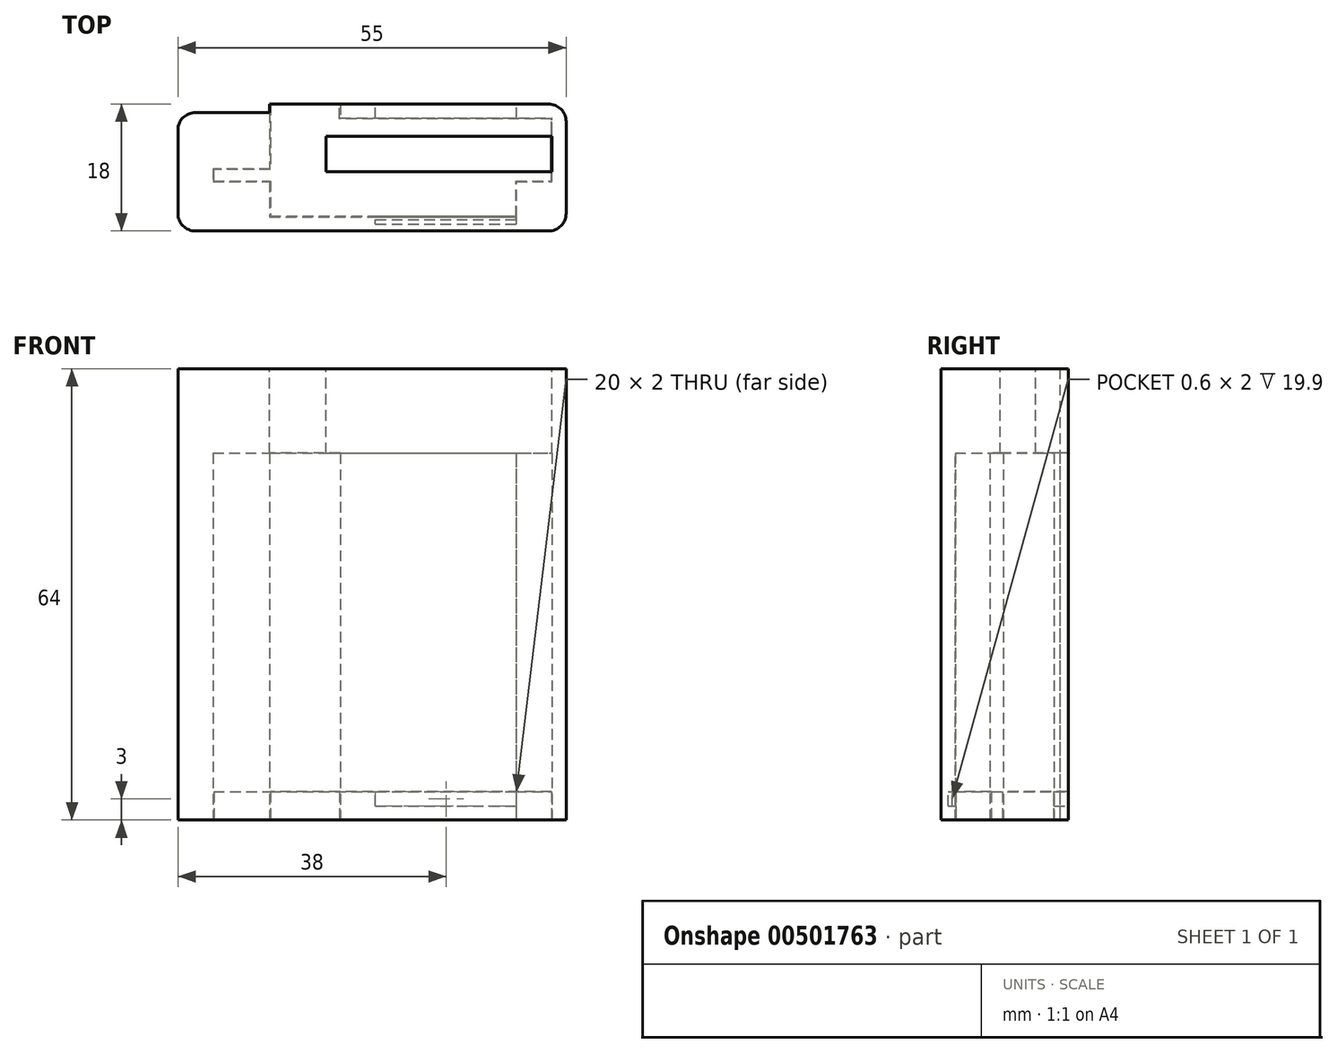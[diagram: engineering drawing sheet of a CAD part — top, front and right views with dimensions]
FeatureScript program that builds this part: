
annotation { "Feature Type Name" : "Feature", "Feature Type Description" : "" }
export const myFeature = defineFeature(function(context is Context, id is Id, definition is map)
    precondition{}
    {
        {
            var Q0;
            Q0=qCreatedBy(makeId("Top.planeOp"),FACE);
            var sketch = newSketch(context, id + "F0", { "sketchPlane" : qUnion([Q0])});
            skLineSegment(sketch, "E0", {"start": v(0, 0) * mm, "end": v(0, 8) * mm});
            skLineSegment(sketch, "E1", {"start": v(0, 8) * mm, "end": v(-8, 8) * mm});
            skLineSegment(sketch, "E2", {"start": v(0, 0) * mm, "end": v(-8, 0) * mm});
            skLineSegment(sketch, "E3", {"start": v(-8, 0) * mm, "end": v(-8, -1.8) * mm});
            skLineSegment(sketch, "E4", {"start": v(-8, -1.8) * mm, "end": v(0, -1.8) * mm});
            skLineSegment(sketch, "E5", {"start": v(0, -1.8) * mm, "end": v(0, -6.8) * mm});
            skLineSegment(sketch, "E6", {"start": v(-8, 8) * mm, "end": v(-13, 8) * mm});
            skLineSegment(sketch, "E7", {"start": v(-13, 8) * mm, "end": v(-13, -6.8) * mm});
            skLineSegment(sketch, "E8", {"start": v(-13, -6.8) * mm, "end": v(-13, -8.8) * mm});
            skLineSegment(sketch, "E9", {"start": v(0, -6.8) * mm, "end": v(40, -6.8) * mm});
            skLineSegment(sketch, "E10", {"start": v(40, -6.8) * mm, "end": v(40, 7.2) * mm});
            skLineSegment(sketch, "E11", {"start": v(0, 0) * mm, "end": v(10, 0) * mm, "construction": true});
            skLineSegment(sketch, "E12", {"start": v(10, 0) * mm, "end": v(10, 7.2) * mm});
            skLineSegment(sketch, "E13", {"start": v(10, 7.2) * mm, "end": v(40, 7.2) * mm});
            skLineSegment(sketch, "E14", {"start": v(-13, -8.8) * mm, "end": v(42, -8.8) * mm});
            skLineSegment(sketch, "E15", {"start": v(42, -8.8) * mm, "end": v(42, 9.2) * mm});
            skLineSegment(sketch, "E16", {"start": v(42, 9.2) * mm, "end": v(10, 9.2) * mm});
            skLineSegment(sketch, "E17", {"start": v(10, 9.2) * mm, "end": v(10, 7.2) * mm});
            skSolve(sketch);
        }
        {
            var Q0;
            Q0=makeQuery(id+"F0.imprint","IMPRINT",FACE,{"disambiguationData":[TD([[makeQuery(id+"F0.imprint","IMPRINT",EDGE,{"derivedFrom":sQuery(id+"F0.wireOp",EDGE,"E0")}),1.0]])]});
            extrude(context, id + "F1", {"entities" : qUnion([Q0]), "depth" : 60 * mm});
        }
        {
            var Q0;
            Q0=makeQuery(id+"F1.opExtrude","CAP_FACE",FACE,{"disambiguationData":[OSD([sQuery(id+"F0.wireOp",EDGE,"E0"),sQuery(id+"F0.wireOp",EDGE,"E1"),sQuery(id+"F0.wireOp",EDGE,"E2"),sQuery(id+"F0.wireOp",EDGE,"E3"),sQuery(id+"F0.wireOp",EDGE,"E4"),sQuery(id+"F0.wireOp",EDGE,"E5"),sQuery(id+"F0.wireOp",EDGE,"E6"),sQuery(id+"F0.wireOp",EDGE,"E7"),sQuery(id+"F0.wireOp",EDGE,"E8"),sQuery(id+"F0.wireOp",EDGE,"E9"),sQuery(id+"F0.wireOp",EDGE,"E10"),sQuery(id+"F0.wireOp",EDGE,"E13"),sQuery(id+"F0.wireOp",EDGE,"E14"),sQuery(id+"F0.wireOp",EDGE,"E15"),sQuery(id+"F0.wireOp",EDGE,"E16"),sQuery(id+"F0.wireOp",EDGE,"E17")])],"isStart":false});
            var sketch = newSketch(context, id + "F2", { "sketchPlane" : qUnion([Q0])});
            skLineSegment(sketch, "E18", {"start": v(8, -0.4) * mm, "end": v(40, -0.4) * mm});
            skLineSegment(sketch, "E19", {"start": v(8, -0.4) * mm, "end": v(8, 4.6) * mm});
            skLineSegment(sketch, "E20", {"start": v(8, 4.6) * mm, "end": v(40, 4.6) * mm});
            skLineSegment(sketch, "E21", {"start": v(40, 4.6) * mm, "end": v(40, -0.4) * mm});
            skLineSegment(sketch, "E22", {"start": v(10, 9.2) * mm, "end": v(0, 9.2) * mm});
            skLineSegment(sketch, "E23", {"start": v(0, 9.2) * mm, "end": v(0, 8) * mm});
            skSolve(sketch);
        }
        {
            var Q0;
            {var subQ0=sQuery(id+"F2.wireOp",EDGE,"E18");Q0=makeQuery(id+"F2.imprint","IMPRINT",FACE,{"disambiguationData":[TD([[makeQuery(id+"F2.imprint","IMPRINT",EDGE,{"derivedFrom":subQ0}),-1.0]])]});}
            extrude(context, id + "F3", {"entities" : qUnion([Q0]), "operationType" : NewBodyOperationType.ADD, "oppositeDirection" : true, "depth" : 12 * mm});
        }
        {
            var Q0;
            Q0=makeQuery(id+"F1.opExtrude","SWEPT_EDGE",EDGE,{"disambiguationData":[OSD([sQuery(id+"F0.wireOp",EDGE,"E15"),sQuery(id+"F0.wireOp",EDGE,"E16")])]});
            var Q1;
            Q1=makeQuery(id+"F1.opExtrude","SWEPT_EDGE",EDGE,{"disambiguationData":[OSD([sQuery(id+"F0.wireOp",EDGE,"E14"),sQuery(id+"F0.wireOp",EDGE,"E15")])]});
            var Q2;
            Q2=makeQuery(id+"F1.opExtrude","SWEPT_EDGE",EDGE,{"disambiguationData":[OSD([sQuery(id+"F0.wireOp",EDGE,"E8"),sQuery(id+"F0.wireOp",EDGE,"E14")])]});
            var Q3;
            Q3=makeQuery(id+"F1.opExtrude","SWEPT_EDGE",EDGE,{"disambiguationData":[OSD([sQuery(id+"F0.wireOp",EDGE,"E6"),sQuery(id+"F0.wireOp",EDGE,"E7")])]});
            fillet(context, id + "F4", {"entities" : qUnion([Q0, Q1, Q2, Q3]), "radius" : 2.5 * mm, "tangentPropagation" : true, "allowEdgeOverflow" : false});
        }
        {
            var Q0;
            Q0=makeQuery(id+"F1.opExtrude","CAP_FACE",FACE,{"disambiguationData":[OSD([sQuery(id+"F0.wireOp",EDGE,"E0"),sQuery(id+"F0.wireOp",EDGE,"E1"),sQuery(id+"F0.wireOp",EDGE,"E2"),sQuery(id+"F0.wireOp",EDGE,"E3"),sQuery(id+"F0.wireOp",EDGE,"E4"),sQuery(id+"F0.wireOp",EDGE,"E5"),sQuery(id+"F0.wireOp",EDGE,"E6"),sQuery(id+"F0.wireOp",EDGE,"E7"),sQuery(id+"F0.wireOp",EDGE,"E8"),sQuery(id+"F0.wireOp",EDGE,"E9"),sQuery(id+"F0.wireOp",EDGE,"E10"),sQuery(id+"F0.wireOp",EDGE,"E13"),sQuery(id+"F0.wireOp",EDGE,"E14"),sQuery(id+"F0.wireOp",EDGE,"E15"),sQuery(id+"F0.wireOp",EDGE,"E16"),sQuery(id+"F0.wireOp",EDGE,"E17")])],"isStart":true});
            extrude(context, id + "F5", {"entities" : qUnion([Q0]), "operationType" : NewBodyOperationType.ADD, "depth" : 4 * mm});
        }
        {
            var Q0;
            Q0=makeQuery(id+"F3.opExtrude","CAP_FACE",FACE,{"disambiguationData":[OSD([sQuery(id+"F0.wireOp",EDGE,"E0"),sQuery(id+"F0.wireOp",EDGE,"E2"),sQuery(id+"F0.wireOp",EDGE,"E3"),sQuery(id+"F0.wireOp",EDGE,"E4"),sQuery(id+"F0.wireOp",EDGE,"E5"),sQuery(id+"F0.wireOp",EDGE,"E9"),sQuery(id+"F0.wireOp",EDGE,"E10"),sQuery(id+"F0.wireOp",EDGE,"E13"),sQuery(id+"F0.wireOp",EDGE,"E17"),sQuery(id+"F2.wireOp",EDGE,"E18"),sQuery(id+"F2.wireOp",EDGE,"E19"),sQuery(id+"F2.wireOp",EDGE,"E20"),sQuery(id+"F2.wireOp",EDGE,"E22"),sQuery(id+"F2.wireOp",EDGE,"E23")])],"isStart":false});
            var sketch = newSketch(context, id + "F6", { "sketchPlane" : qUnion([Q0])});
            skLineSegment(sketch, "E24", {"start": v(35, 6.8) * mm, "end": v(35, 1.8) * mm});
            skLineSegment(sketch, "E25.0", {"start": v(0, 1.8) * mm, "end": v(0, 6.8) * mm});
            skLineSegment(sketch, "E26", {"start": v(35, 1.8) * mm, "end": v(40, 1.8) * mm});
            skSolve(sketch);
        }
        {
            var Q0;
            {var subQ0=sQuery(id+"F6.wireOp",EDGE,"E24");Q0=makeQuery(id+"F6.imprint","IMPRINT",FACE,{"disambiguationData":[TD([[makeQuery(id+"F6.imprint","IMPRINT",EDGE,{"derivedFrom":subQ0}),1.0]])]});}
            extrude(context, id + "F7", {"entities" : qUnion([Q0]), "operationType" : NewBodyOperationType.ADD, "depth" : 52 * mm});
        }
        {
            var Q0;
            {var subQ0=sQuery(id+"F0.wireOp",EDGE,"E16");Q0=makeQuery(id+"F5.boolean.opBoolean","MERGE",FACE,{"derivedFrom":[makeQuery(id+"F3.boolean.opBoolean","MERGE",FACE,{"derivedFrom":[makeQuery(id+"F1.opExtrude","SWEPT_FACE",FACE,{"disambiguationData":[OSD([subQ0])]}),makeQuery(id+"F3.opExtrude","SWEPT_FACE",FACE,{"disambiguationData":[OSD([sQuery(id+"F2.wireOp",EDGE,"E22")])]})]}),makeQuery(id+"F5.opExtrude","SWEPT_FACE",FACE,{"disambiguationData":[OSD([subQ0])]})]});}
            var sketch = newSketch(context, id + "F8", { "sketchPlane" : qUnion([Q0])});
            skLineSegment(sketch, "E27.bottom", {"start": v(-15, -2) * mm, "end": v(-35, -2) * mm});
            skLineSegment(sketch, "E27.top", {"start": v(-15, 0) * mm, "end": v(-35, 0) * mm});
            skLineSegment(sketch, "E27.left", {"start": v(-15, -2) * mm, "end": v(-15, 0) * mm});
            skLineSegment(sketch, "E27.right", {"start": v(-35, -2) * mm, "end": v(-35, 0) * mm});
            skSolve(sketch);
        }
        {
            var Q0;
            Q0 = qSketchRegion(id + "F8", true);
            extrude(context, id + "F9", {"entities" : qUnion([Q0]), "operationType" : NewBodyOperationType.REMOVE, "oppositeDirection" : true, "depth" : 17 * mm});
        }
        {
            var Q0;
            {var subQ0=sQuery(id+"F0.wireOp",EDGE,"E16");Q0=makeQuery(id+"F5.boolean.opBoolean","MERGE",FACE,{"derivedFrom":[makeQuery(id+"F3.boolean.opBoolean","MERGE",FACE,{"derivedFrom":[makeQuery(id+"F1.opExtrude","SWEPT_FACE",FACE,{"disambiguationData":[OSD([subQ0])]}),makeQuery(id+"F3.opExtrude","SWEPT_FACE",FACE,{"disambiguationData":[OSD([sQuery(id+"F2.wireOp",EDGE,"E22")])]})]}),makeQuery(id+"F5.opExtrude","SWEPT_FACE",FACE,{"disambiguationData":[OSD([subQ0])]})]});}
            var sketch = newSketch(context, id + "F10", { "sketchPlane" : qUnion([Q0])});
            skLineSegment(sketch, "E28.bottom", {"start": v(-35, 0) * mm, "end": v(-15, 0) * mm});
            skLineSegment(sketch, "E28.top", {"start": v(-35, -2) * mm, "end": v(-15, -2) * mm});
            skLineSegment(sketch, "E28.left", {"start": v(-35, 0) * mm, "end": v(-35, -2) * mm});
            skLineSegment(sketch, "E28.right", {"start": v(-15, 0) * mm, "end": v(-15, -2) * mm});
            skSolve(sketch);
        }
        {
            var Q0;
            {var subQ0=sQuery(id+"F0.wireOp",EDGE,"E10");var subQ1=sQuery(id+"F0.wireOp",EDGE,"E9");Q0=makeQuery(id+"F7.boolean.opBoolean","MERGE",FACE,{"derivedFrom":[makeQuery(id+"F5.opExtrude","CAP_FACE",FACE,{"disambiguationData":[OSD([sQuery(id+"F0.wireOp",EDGE,"E0"),sQuery(id+"F0.wireOp",EDGE,"E1"),sQuery(id+"F0.wireOp",EDGE,"E2"),sQuery(id+"F0.wireOp",EDGE,"E3"),sQuery(id+"F0.wireOp",EDGE,"E4"),sQuery(id+"F0.wireOp",EDGE,"E5"),sQuery(id+"F0.wireOp",EDGE,"E6"),sQuery(id+"F0.wireOp",EDGE,"E7"),sQuery(id+"F0.wireOp",EDGE,"E8"),subQ1,subQ0,sQuery(id+"F0.wireOp",EDGE,"E13"),sQuery(id+"F0.wireOp",EDGE,"E14"),sQuery(id+"F0.wireOp",EDGE,"E15"),sQuery(id+"F0.wireOp",EDGE,"E16"),sQuery(id+"F0.wireOp",EDGE,"E17")])],"isStart":false}),makeQuery(id+"F7.opExtrude","CAP_FACE",FACE,{"disambiguationData":[OSD([subQ1,subQ0,sQuery(id+"F6.wireOp",EDGE,"E24"),sQuery(id+"F6.wireOp",EDGE,"E26")])],"isStart":false})]});}
            var sketch = newSketch(context, id + "F11", { "sketchPlane" : qUnion([Q0])});
            skLineSegment(sketch, "E29", {"start": v(40, -7.2) * mm, "end": v(10, -7.2) * mm});
            skLineSegment(sketch, "E30", {"start": v(10, -7.2) * mm, "end": v(10, -9.2) * mm});
            skLineSegment(sketch, "E31", {"start": v(10, -9.2) * mm, "end": v(0, -9.2) * mm});
            skLineSegment(sketch, "E32", {"start": v(0, -9.2) * mm, "end": v(0, -8) * mm});
            skLineSegment(sketch, "E33", {"start": v(0, -8) * mm, "end": v(0, 0) * mm});
            skLineSegment(sketch, "E34", {"start": v(0, 0) * mm, "end": v(-8, 0) * mm});
            skLineSegment(sketch, "E35", {"start": v(-8, 0) * mm, "end": v(-8, 1.8) * mm});
            skLineSegment(sketch, "E36", {"start": v(-8, 1.8) * mm, "end": v(0, 1.8) * mm});
            skLineSegment(sketch, "E37", {"start": v(0, 1.8) * mm, "end": v(0, 6.8) * mm});
            skLineSegment(sketch, "E38", {"start": v(0, 6.8) * mm, "end": v(35, 6.8) * mm});
            skLineSegment(sketch, "E39", {"start": v(35, 6.8) * mm, "end": v(35, 1.8) * mm});
            skLineSegment(sketch, "E40", {"start": v(35, 1.8) * mm, "end": v(40, 1.8) * mm});
            skLineSegment(sketch, "E41", {"start": v(40, 1.8) * mm, "end": v(40, -7.2) * mm});
            skLineSegment(sketch, "E42.0", {"start": v(9.9, -7.1) * mm, "end": v(9.9, -9.1) * mm});
            skLineSegment(sketch, "E42.1", {"start": v(39.9, -7.1) * mm, "end": v(9.9, -7.1) * mm});
            skLineSegment(sketch, "E42.2", {"start": v(9.9, -9.1) * mm, "end": v(0.1, -9.1) * mm});
            skLineSegment(sketch, "E42.3", {"start": v(39.9, 1.7) * mm, "end": v(39.9, -7.1) * mm});
            skLineSegment(sketch, "E42.4", {"start": v(34.9, 1.7) * mm, "end": v(39.9, 1.7) * mm});
            skLineSegment(sketch, "E42.5", {"start": v(0.1, -9.1) * mm, "end": v(0.1, -0.2) * mm});
            skLineSegment(sketch, "E42.6", {"start": v(0.1, -0.2) * mm, "end": v(0.1, 0.1) * mm});
            skLineSegment(sketch, "E42.7", {"start": v(0.1, 6.7) * mm, "end": v(34.9, 6.7) * mm});
            skLineSegment(sketch, "E42.8", {"start": v(34.9, 6.7) * mm, "end": v(34.9, 1.7) * mm});
            skLineSegment(sketch, "E43", {"start": v(-8, 0) * mm, "end": v(0, 0) * mm});
            skLineSegment(sketch, "E44", {"start": v(-8, 1.8) * mm, "end": v(-8, 0) * mm});
            skLineSegment(sketch, "E45.0", {"start": v(-7.9, 1.7) * mm, "end": v(0.1, 1.7) * mm});
            skLineSegment(sketch, "E45.1", {"start": v(-7.9, 1.7) * mm, "end": v(-7.9, 0.1) * mm});
            skLineSegment(sketch, "E45.2", {"start": v(0.1, 0.1) * mm, "end": v(-7.9, 0.1) * mm});
            skLineSegment(sketch, "E46.trimOffspring", {"start": v(0.1, 1.7) * mm, "end": v(0.1, 6.7) * mm});
            skSolve(sketch);
        }
        {
            var Q0;
            Q0=makeQuery(id+"F11.imprint","IMPRINT",FACE,{"disambiguationData":[TD([[makeQuery(id+"F11.imprint","IMPRINT",EDGE,{"derivedFrom":sQuery(id+"F11.wireOp",EDGE,"E42.0")}),-1.0]])]});
            var Q1;
            Q1 = qSketchRegion(id + "F13", true);
            extrude(context, id + "F12", {"entities" : qUnion([Q0, Q1]), "oppositeDirection" : true, "depth" : 4 * mm});
        }
        {
            var Q0;
            Q0=makeQuery(id+"F12.opExtrude","SWEPT_FACE",FACE,{"disambiguationData":[OSD([sQuery(id+"F11.wireOp",EDGE,"E42.1")])]});
            var sketch = newSketch(context, id + "F13", { "sketchPlane" : qUnion([Q0])});
            skLineSegment(sketch, "E47.0.0", {"start": v(-15, -2) * mm, "end": v(-15, 0) * mm});
            skLineSegment(sketch, "E47.0.1", {"start": v(-15, 0) * mm, "end": v(-35, 0) * mm});
            skLineSegment(sketch, "E47.0.2", {"start": v(-35, 0) * mm, "end": v(-35, -2) * mm});
            skLineSegment(sketch, "E47.0.3", {"start": v(-35, -2) * mm, "end": v(-15, -2) * mm});
            skSolve(sketch);
        }
        {
            var Q0;
            Q0=makeQuery(id+"F12.opExtrude","SWEPT_FACE",FACE,{"disambiguationData":[OSD([sQuery(id+"F11.wireOp",EDGE,"E42.7")])]});
            var sketch = newSketch(context, id + "F14", { "sketchPlane" : qUnion([Q0])});
            skLineSegment(sketch, "E48.0", {"start": v(15, -2) * mm, "end": v(35, -2) * mm});
            skLineSegment(sketch, "E48.2", {"start": v(15, -2) * mm, "end": v(15, 0) * mm});
            skSolve(sketch);
        }
        {
            var Q0;
            {var subQ0=sQuery(id+"F14.wireOp",EDGE,"E48.2");Q0=makeQuery(id+"F14.imprint","IMPRINT",FACE,{"disambiguationData":[TD([[makeQuery(id+"F14.imprint","IMPRINT",EDGE,{"derivedFrom":subQ0}),-1.0]])]});}
            extrude(context, id + "F15", {"entities" : qUnion([Q0]), "operationType" : NewBodyOperationType.ADD, "depth" : .5 * mm});
        }
    });
